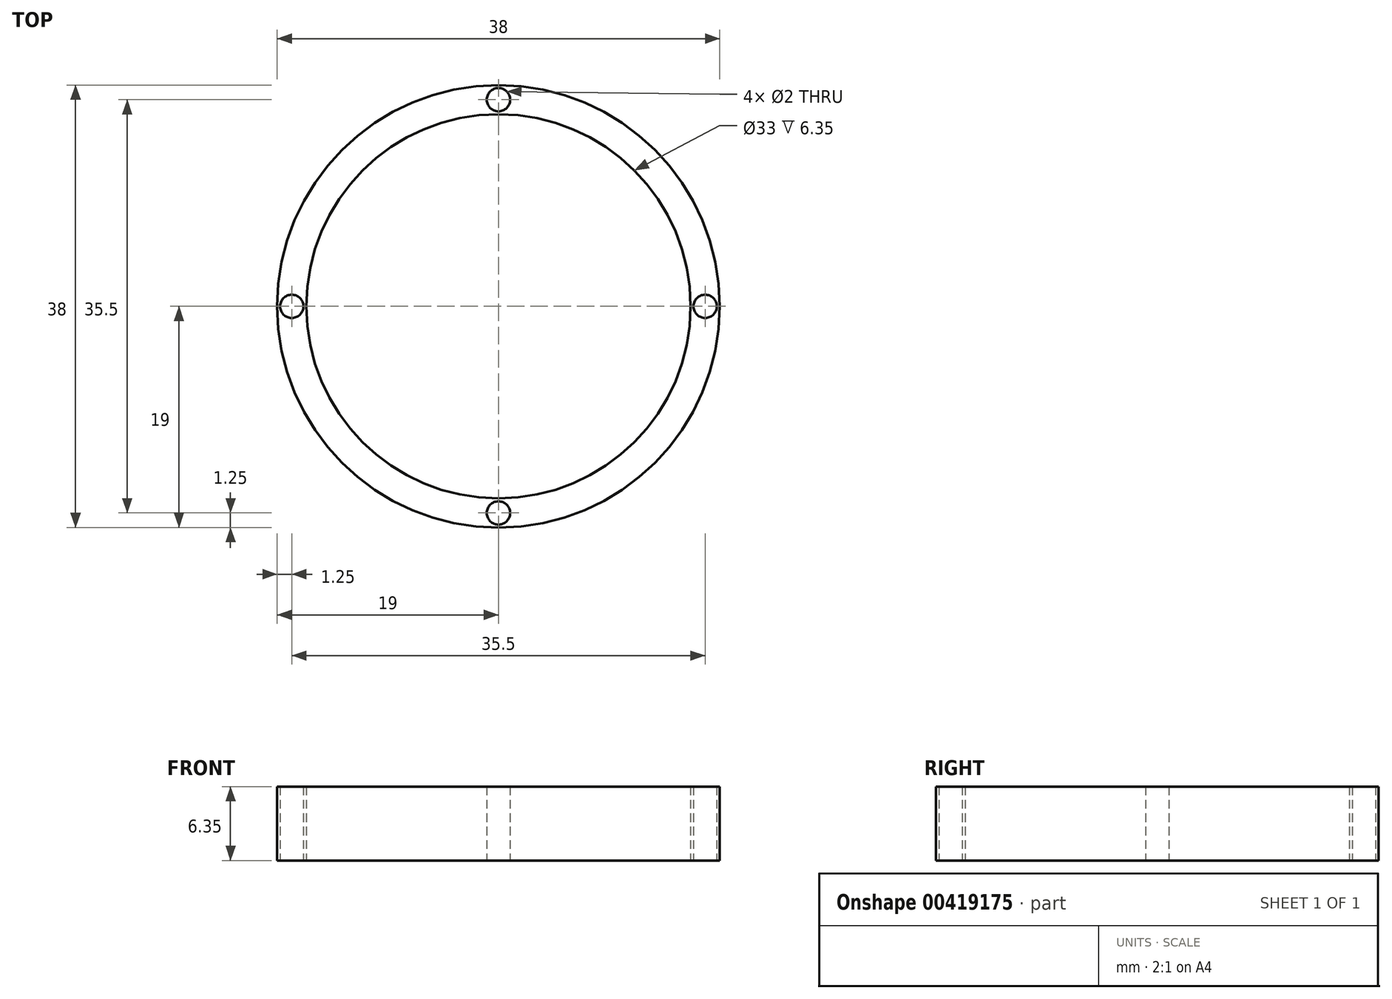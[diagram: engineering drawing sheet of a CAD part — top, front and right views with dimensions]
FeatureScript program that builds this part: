
annotation { "Feature Type Name" : "Feature", "Feature Type Description" : "" }
export const myFeature = defineFeature(function(context is Context, id is Id, definition is map)
    precondition{}
    {
        {
            var Q0;
            Q0=qCreatedBy(makeId("Top.planeOp"),FACE);
            var sketch = newSketch(context, id + "F0", { "sketchPlane" : qUnion([Q0])});
            skCircle(sketch, "E0", {"center": v(0, 0) * mm, "radius": 16.5 * mm});
            skCircle(sketch, "E1", {"center": v(0, 0) * mm, "radius": 19 * mm});
            skLineSegment(sketch, "E2", {"start": v(0, 0) * mm, "end": v(-19, 0) * mm});
            skLineSegment(sketch, "E3", {"start": v(-19, 0) * mm, "end": v(-16.5, 0) * mm});
            skLineSegment(sketch, "E4", {"start": v(-16.5, 0) * mm, "end": v(-17.75, 0) * mm});
            skLineSegment(sketch, "E5", {"start": v(-17.75, 0) * mm, "end": v(-17.75, -0.89) * mm});
            skCircle(sketch, "E6", {"center": v(-17.75, 0) * mm, "radius": 1 * mm});
            skCircle(sketch, "E7.1.0", {"center": v(0, -17.75) * mm, "radius": 1 * mm});
            skCircle(sketch, "E7.2.0", {"center": v(17.75, 0) * mm, "radius": 1 * mm});
            skCircle(sketch, "E8.1.3.0", {"center": v(0, 17.75) * mm, "radius": 1 * mm});
            skSolve(sketch);
        }
        {
            var Q0;
            Q0 = qSketchRegion(id + "F0", true);
            extrude(context, id + "F1", {"entities" : qUnion([Q0]), "depth" : 6.35 * mm});
        }
    });
